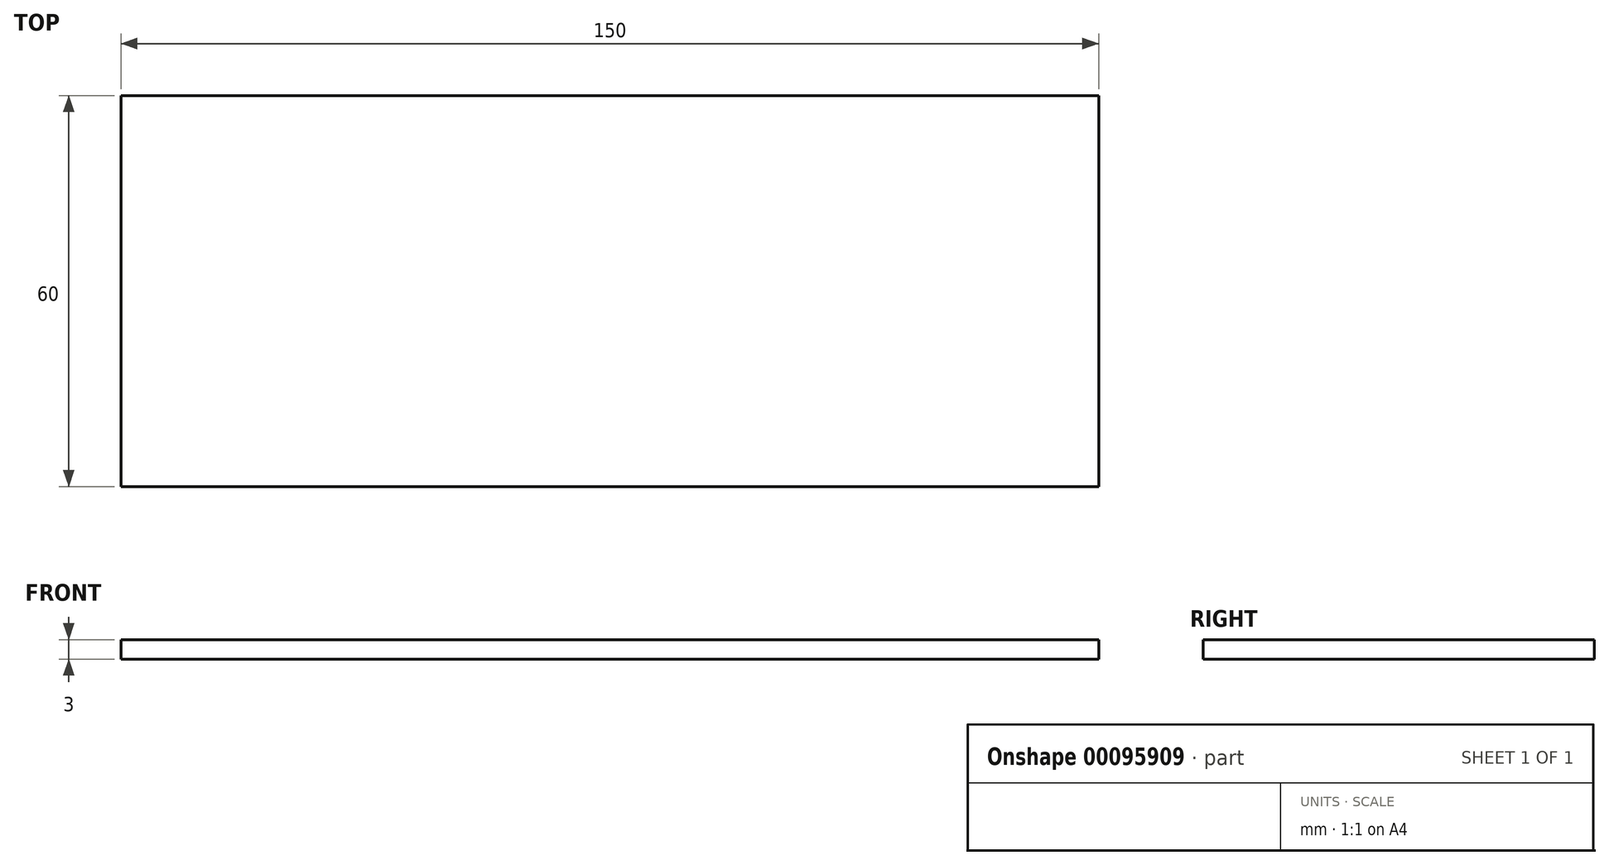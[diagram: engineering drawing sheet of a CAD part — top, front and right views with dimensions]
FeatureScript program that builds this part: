
annotation { "Feature Type Name" : "Feature", "Feature Type Description" : "" }
export const myFeature = defineFeature(function(context is Context, id is Id, definition is map)
    precondition{}
    {
        {
            var Q0;
            Q0=qCreatedBy(makeId("Top.planeOp"),FACE);
            var sketch = newSketch(context, id + "F0", { "sketchPlane" : qUnion([Q0])});
            skLineSegment(sketch, "E0.bottom", {"start": v(75, -30) * mm, "end": v(-75, -30) * mm});
            skLineSegment(sketch, "E0.top", {"start": v(75, 30) * mm, "end": v(-75, 30) * mm});
            skLineSegment(sketch, "E0.left", {"start": v(75, -30) * mm, "end": v(75, 30) * mm});
            skLineSegment(sketch, "E0.right", {"start": v(-75, -30) * mm, "end": v(-75, 30) * mm});
            skPoint(sketch, "E0.middle", {"position": v(0, 0) * mm});
            skSolve(sketch);
        }
        {
            var Q0;
            Q0 = qSketchRegion(id + "F0", true);
            extrude(context, id + "F1", {"entities" : qUnion([Q0]), "depth" : 3 * mm});
        }
    });
